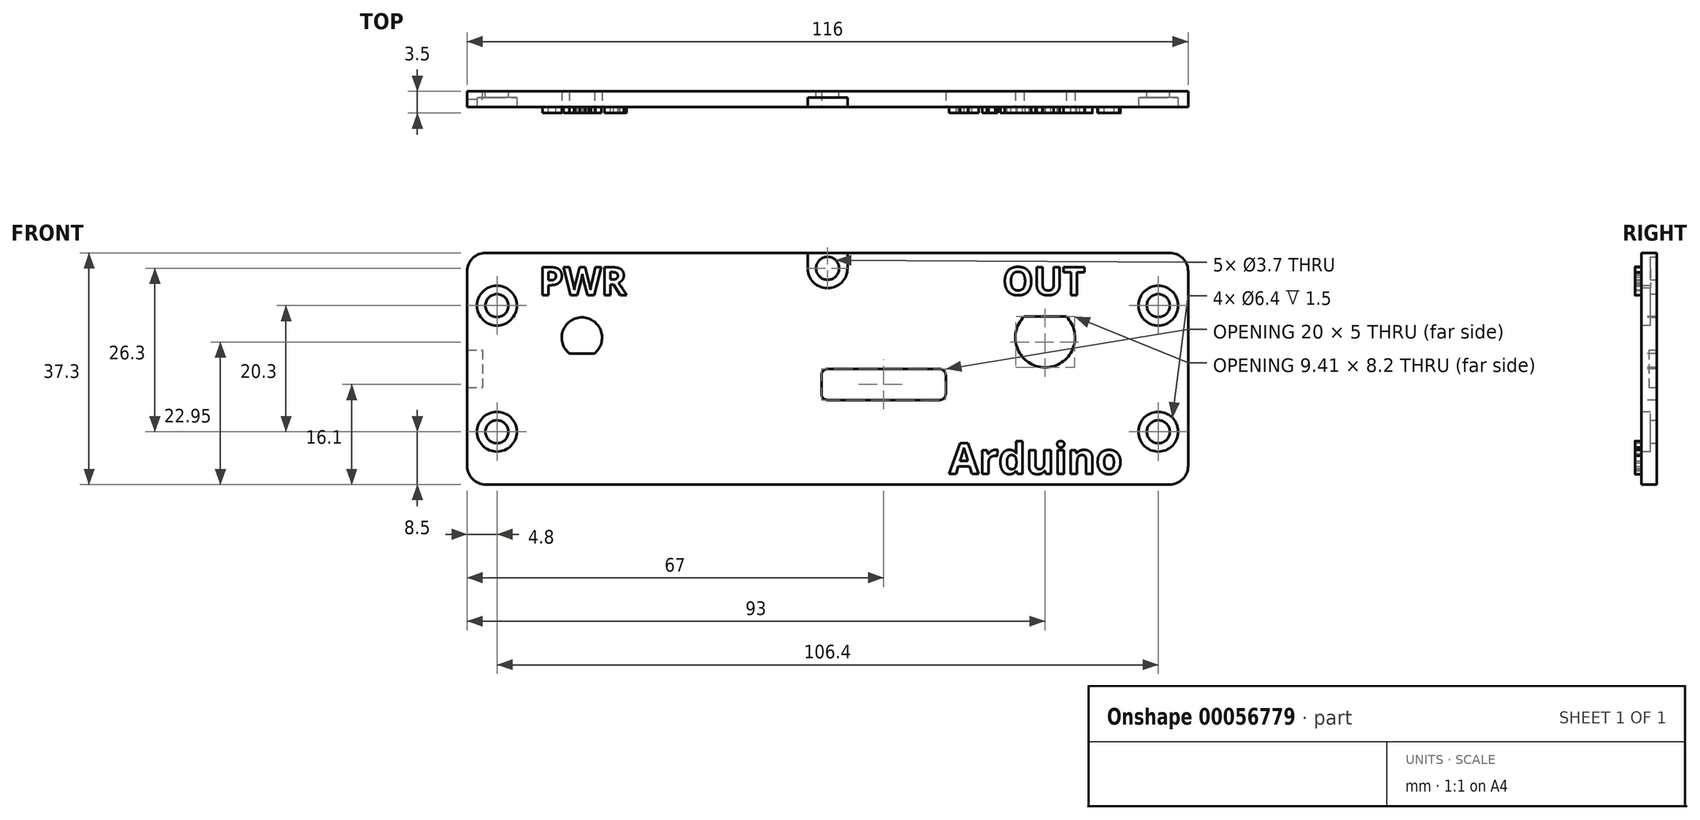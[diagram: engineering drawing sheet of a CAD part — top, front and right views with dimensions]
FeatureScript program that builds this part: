
annotation { "Feature Type Name" : "Feature", "Feature Type Description" : "" }
export const myFeature = defineFeature(function(context is Context, id is Id, definition is map)
    precondition{}
    {
        {
            var Q0;
            Q0=qCreatedBy(makeId("Front.planeOp"),FACE);
            var sketch = newSketch(context, id + "F0", { "sketchPlane" : qUnion([Q0])});
            skLineSegment(sketch, "E0.bottom", {"start": v(-55, 18.65) * mm, "end": v(55, 18.65) * mm});
            skLineSegment(sketch, "E0.top", {"start": v(-55, -18.65) * mm, "end": v(55, -18.65) * mm});
            skLineSegment(sketch, "E0.left", {"start": v(-58, 15.65) * mm, "end": v(-58, -15.65) * mm});
            skLineSegment(sketch, "E0.right", {"start": v(58, 15.65) * mm, "end": v(58, -15.65) * mm});
            skPoint(sketch, "E1.visualSharp", {"position": v(-58, 18.65) * mm});
            skArc(sketch, "E1.filletArc", {"start": v(-55, 18.65) * mm, "mid": v(-57.12, 17.77) * mm, "end": v(-58, 15.65) * mm});
            skPoint(sketch, "E2.visualSharp", {"position": v(58, 18.65) * mm});
            skArc(sketch, "E2.filletArc", {"start": v(58, 15.65) * mm, "mid": v(57.12, 17.77) * mm, "end": v(55, 18.65) * mm});
            skPoint(sketch, "E3.visualSharp", {"position": v(58, -18.65) * mm});
            skArc(sketch, "E3.filletArc", {"start": v(55, -18.65) * mm, "mid": v(57.12, -17.77) * mm, "end": v(58, -15.65) * mm});
            skPoint(sketch, "E4.visualSharp", {"position": v(-58, -18.65) * mm});
            skArc(sketch, "E4.filletArc", {"start": v(-58, -15.65) * mm, "mid": v(-57.12, -17.77) * mm, "end": v(-55, -18.65) * mm});
            skCircle(sketch, "E5", {"center": v(-53.2, 10.15) * mm, "radius": 1.85 * mm});
            skCircle(sketch, "E6", {"center": v(53.2, 10.15) * mm, "radius": 1.85 * mm});
            skCircle(sketch, "E7", {"center": v(-53.2, -10.15) * mm, "radius": 1.85 * mm});
            skCircle(sketch, "E8", {"center": v(53.2, -10.15) * mm, "radius": 1.85 * mm});
            skCircle(sketch, "E9", {"center": v(0, 16.15) * mm, "radius": 1.85 * mm});
            skSolve(sketch);
        }
        {
            var Q0;
            Q0=makeQuery(id+"F0.imprint","IMPRINT",FACE,{"disambiguationData":[TD([[makeQuery(id+"F0.imprint","IMPRINT",EDGE,{"derivedFrom":sQuery(id+"F0.wireOp",EDGE,"E0.bottom")}),-1.0]])]});
            extrude(context, id + "F1", {"entities" : qUnion([Q0]), "depth" : 2.5 * mm});
        }
        {
            var Q0;
            Q0=makeQuery(id+"F1.opExtrude","CAP_FACE",FACE,{"disambiguationData":[OSD([sQuery(id+"F0.wireOp",EDGE,"E0.bottom"),sQuery(id+"F0.wireOp",EDGE,"E0.top"),sQuery(id+"F0.wireOp",EDGE,"E0.left"),sQuery(id+"F0.wireOp",EDGE,"E0.right"),sQuery(id+"F0.wireOp",EDGE,"E1.filletArc"),sQuery(id+"F0.wireOp",EDGE,"E2.filletArc"),sQuery(id+"F0.wireOp",EDGE,"E3.filletArc"),sQuery(id+"F0.wireOp",EDGE,"E4.filletArc"),sQuery(id+"F0.wireOp",EDGE,"E5"),sQuery(id+"F0.wireOp",EDGE,"E6"),sQuery(id+"F0.wireOp",EDGE,"E7"),sQuery(id+"F0.wireOp",EDGE,"E8")])],"isStart":false});
            var sketch = newSketch(context, id + "F2", { "sketchPlane" : qUnion([Q0])});
            skCircle(sketch, "E10", {"center": v(-53.2, 10.15) * mm, "radius": 3.2 * mm});
            skCircle(sketch, "E11", {"center": v(53.2, 10.15) * mm, "radius": 3.2 * mm});
            skCircle(sketch, "E12", {"center": v(-53.2, -10.15) * mm, "radius": 3.2 * mm});
            skCircle(sketch, "E13", {"center": v(53.2, -10.15) * mm, "radius": 3.2 * mm});
            skArc(sketch, "E14", {"start": v(-3.2, 16.15) * mm, "mid": v(0, 12.95) * mm, "end": v(3.2, 16.15) * mm});
            skLineSegment(sketch, "E15", {"start": v(-3.2, 16.15) * mm, "end": v(-3.2, 18.65) * mm});
            skLineSegment(sketch, "E16", {"start": v(3.2, 16.15) * mm, "end": v(3.2, 18.65) * mm});
            skLineSegment(sketch, "E17", {"start": v(-3.2, 18.65) * mm, "end": v(3.2, 18.65) * mm});
            skSolve(sketch);
        }
        {
            var Q0;
            Q0=qSketchRegion(id+"F2",true);
            extrude(context, id + "F3", {"entities" : qUnion([Q0]), "operationType" : NewBodyOperationType.REMOVE, "oppositeDirection" : true, "depth" : 1.5 * mm});
        }
        {
            var Q0;
            Q0=makeQuery(id+"F1.opExtrude","CAP_FACE",FACE,{"disambiguationData":[OSD([sQuery(id+"F0.wireOp",EDGE,"E0.bottom"),sQuery(id+"F0.wireOp",EDGE,"E0.top"),sQuery(id+"F0.wireOp",EDGE,"E0.left"),sQuery(id+"F0.wireOp",EDGE,"E0.right"),sQuery(id+"F0.wireOp",EDGE,"E1.filletArc"),sQuery(id+"F0.wireOp",EDGE,"E2.filletArc"),sQuery(id+"F0.wireOp",EDGE,"E3.filletArc"),sQuery(id+"F0.wireOp",EDGE,"E4.filletArc"),sQuery(id+"F0.wireOp",EDGE,"E5"),sQuery(id+"F0.wireOp",EDGE,"E6"),sQuery(id+"F0.wireOp",EDGE,"E7"),sQuery(id+"F0.wireOp",EDGE,"E8")])],"isStart":true});
            var sketch = newSketch(context, id + "F4", { "sketchPlane" : qUnion([Q0])});
            skLineSegment(sketch, "E18.bottom", {"start": v(58, 3) * mm, "end": v(55.5, 3) * mm});
            skLineSegment(sketch, "E18.top", {"start": v(58, -3) * mm, "end": v(55.5, -3) * mm});
            skLineSegment(sketch, "E18.left", {"start": v(58, 3) * mm, "end": v(58, -3) * mm});
            skLineSegment(sketch, "E18.right", {"start": v(55.5, 3) * mm, "end": v(55.5, -3) * mm});
            skSolve(sketch);
        }
        {
            var Q0;
            Q0=qSketchRegion(id+"F4",true);
            extrude(context, id + "F5", {"entities" : qUnion([Q0]), "operationType" : NewBodyOperationType.REMOVE, "oppositeDirection" : true, "depth" : 1.25 * mm});
        }
        {
            var Q0;
            Q0=makeQuery(id+"F1.opExtrude","CAP_FACE",FACE,{"disambiguationData":[OSD([sQuery(id+"F0.wireOp",EDGE,"E0.bottom"),sQuery(id+"F0.wireOp",EDGE,"E0.top"),sQuery(id+"F0.wireOp",EDGE,"E0.left"),sQuery(id+"F0.wireOp",EDGE,"E0.right"),sQuery(id+"F0.wireOp",EDGE,"E1.filletArc"),sQuery(id+"F0.wireOp",EDGE,"E2.filletArc"),sQuery(id+"F0.wireOp",EDGE,"E3.filletArc"),sQuery(id+"F0.wireOp",EDGE,"E4.filletArc"),sQuery(id+"F0.wireOp",EDGE,"E5"),sQuery(id+"F0.wireOp",EDGE,"E6"),sQuery(id+"F0.wireOp",EDGE,"E7"),sQuery(id+"F0.wireOp",EDGE,"E8")])],"isStart":false});
            var sketch = newSketch(context, id + "F6", { "sketchPlane" : qUnion([Q0])});
            skLineSegment(sketch, "E19", {"start": v(-63.46, 5) * mm, "end": v(64.15, 5) * mm, "construction": true});
            skArc(sketch, "E20", {"start": v(-37.52, 2.45) * mm, "mid": v(-39.53, 8.25) * mm, "end": v(-41.55, 2.45) * mm});
            skLineSegment(sketch, "E21", {"start": v(-48, 18.65) * mm, "end": v(-48, -12.65) * mm, "construction": true});
            skLineSegment(sketch, "E22", {"start": v(-48, -12.65) * mm, "end": v(48, -12.65) * mm, "construction": true});
            skLineSegment(sketch, "E23", {"start": v(48, -12.65) * mm, "end": v(48, 18.65) * mm, "construction": true});
            skLineSegment(sketch, "E24", {"start": v(-41.55, 2.45) * mm, "end": v(-37.52, 2.45) * mm});
            skLineSegment(sketch, "E25", {"start": v(-42.3, 8.25) * mm, "end": v(6.57, 8.25) * mm, "construction": true});
            skLineSegment(sketch, "E26", {"start": v(-63, -5.05) * mm, "end": v(39.3, -5.05) * mm, "construction": true});
            skArc(sketch, "E27", {"start": v(31.61, 8.4) * mm, "mid": v(35, 0.2) * mm, "end": v(38.39, 8.4) * mm});
            skLineSegment(sketch, "E28", {"start": v(31.61, 8.4) * mm, "end": v(38.39, 8.4) * mm});
            skLineSegment(sketch, "E29", {"start": v(13.35, 0.2) * mm, "end": v(48.07, 0.2) * mm, "construction": true});
            skLineSegment(sketch, "E30.bottom", {"start": v(0, -5.05) * mm, "end": v(18, -5.05) * mm});
            skLineSegment(sketch, "E30.top", {"start": v(0, -0.05) * mm, "end": v(18, -0.05) * mm});
            skLineSegment(sketch, "E30.left", {"start": v(-1, -4.05) * mm, "end": v(-1, -1.05) * mm});
            skLineSegment(sketch, "E30.right", {"start": v(19, -4.05) * mm, "end": v(19, -1.05) * mm});
            skPoint(sketch, "E31.visualSharp", {"position": v(-1, -0.05) * mm});
            skArc(sketch, "E31.filletArc", {"start": v(0, -0.05) * mm, "mid": v(-0.7, -0.34) * mm, "end": v(-1, -1.05) * mm});
            skPoint(sketch, "E32.visualSharp", {"position": v(19, -0.05) * mm});
            skArc(sketch, "E32.filletArc", {"start": v(19, -1.05) * mm, "mid": v(18.7, -0.34) * mm, "end": v(18, -0.05) * mm});
            skPoint(sketch, "E33.visualSharp", {"position": v(19, -5.05) * mm});
            skArc(sketch, "E33.filletArc", {"start": v(18, -5.05) * mm, "mid": v(18.7, -4.76) * mm, "end": v(19, -4.05) * mm});
            skPoint(sketch, "E34.visualSharp", {"position": v(-1, -5.05) * mm});
            skArc(sketch, "E34.filletArc", {"start": v(-1, -4.05) * mm, "mid": v(-0.7, -4.76) * mm, "end": v(0, -5.05) * mm});
            skSolve(sketch);
        }
        {
            var Q0;
            Q0=qSketchRegion(id+"F6",true);
            extrude(context, id + "F7", {"entities" : qUnion([Q0]), "operationType" : NewBodyOperationType.REMOVE, "endBound" : BoundingType.THROUGH_ALL, "oppositeDirection" : true, "depth" : 25 * mm});
        }
        {
            var Q0;
            Q0=makeQuery(id+"F1.opExtrude","CAP_FACE",FACE,{"disambiguationData":[OSD([sQuery(id+"F0.wireOp",EDGE,"E0.bottom"),sQuery(id+"F0.wireOp",EDGE,"E0.top"),sQuery(id+"F0.wireOp",EDGE,"E0.left"),sQuery(id+"F0.wireOp",EDGE,"E0.right"),sQuery(id+"F0.wireOp",EDGE,"E1.filletArc"),sQuery(id+"F0.wireOp",EDGE,"E2.filletArc"),sQuery(id+"F0.wireOp",EDGE,"E3.filletArc"),sQuery(id+"F0.wireOp",EDGE,"E4.filletArc"),sQuery(id+"F0.wireOp",EDGE,"E5"),sQuery(id+"F0.wireOp",EDGE,"E6"),sQuery(id+"F0.wireOp",EDGE,"E7"),sQuery(id+"F0.wireOp",EDGE,"E8")])],"isStart":false});
            var sketch = newSketch(context, id + "F8", { "sketchPlane" : qUnion([Q0])});
            skText(sketch, "E35", { "text": "PWR", "fontName": "OpenSans-Bold.ttf"});
            skText(sketch, "E36", { "text": "OUT", "fontName": "OpenSans-Bold.ttf"});
            const initialGuessF8  = {"E35": [-0.0464, 0.01186, 1, 0, 0.0045], "E36": [0.02815, 0.01186, 1, 0, 0.0045]};
            skSetInitialGuess(sketch, initialGuessF8);
            skSolve(sketch);
        }
        {
            var Q0;
            Q0=qSketchRegion(id+"F8",true);
            extrude(context, id + "F9", {"entities" : qUnion([Q0]), "operationType" : NewBodyOperationType.ADD, "depth" : 1 * mm});
        }
        {
            var Q0;
            {var subQ70=sQuery(id+"F0.wireOp",EDGE,"E0.right");var subQ114=sQuery(id+"F0.wireOp",EDGE,"E3.filletArc");var subQ120=sQuery(id+"F0.wireOp",EDGE,"E4.filletArc");var subQ132=sQuery(id+"F0.wireOp",EDGE,"E1.filletArc");var subQ140=sQuery(id+"F0.wireOp",EDGE,"E0.top");var subQ143=sQuery(id+"F0.wireOp",EDGE,"E0.left");var subQ152=sQuery(id+"F0.wireOp",EDGE,"E2.filletArc");var subQ182=sQuery(id+"F0.wireOp",EDGE,"E0.bottom");var subQ183=makeQuery(id+"F1.opExtrude","SWEPT_FACE",FACE,{"disambiguationData":[OSD([subQ182])]});Q0=makeQuery(id+"Fu2jKsRN7ARvOCH_1.boolean.opBoolean","SPLIT",FACE,{"disambiguationData":[TD([subQ183])],"derivedFrom":makeQuery(id+"F9.boolean.opBoolean","SPLIT",FACE,{"disambiguationData":[TD([subQ183])],"derivedFrom":makeQuery(id+"F1.opExtrude","CAP_FACE",FACE,{"disambiguationData":[OSD([subQ182,subQ140,subQ143,subQ70,subQ132,subQ152,subQ114,subQ120,sQuery(id+"F0.wireOp",EDGE,"E5"),sQuery(id+"F0.wireOp",EDGE,"E6"),sQuery(id+"F0.wireOp",EDGE,"E7"),sQuery(id+"F0.wireOp",EDGE,"E8")])],"isStart":false})})});}
            var sketch = newSketch(context, id + "F10", { "sketchPlane" : qUnion([Q0])});
            skText(sketch, "E37", { "text": "Arduino", "fontName": "OpenSans-Bold.ttf"});
            const initialGuessF10  = {"E37": [0.01954, -0.01693, 1, 0, 0.005]};
            skSetInitialGuess(sketch, initialGuessF10);
            skSolve(sketch);
        }
        {
            var Q0;
            Q0=qSketchRegion(id+"F10",true);
            extrude(context, id + "F11", {"entities" : qUnion([Q0]), "operationType" : NewBodyOperationType.ADD, "depth" : 1 * mm});
        }
    });
